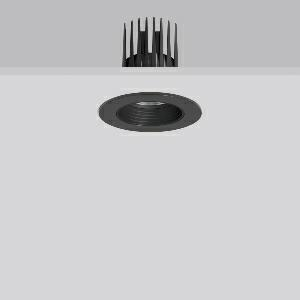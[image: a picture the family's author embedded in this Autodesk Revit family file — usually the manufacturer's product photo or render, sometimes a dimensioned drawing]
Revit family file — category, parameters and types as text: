
# Revit family: heledon_mini_e_901746_003_76_7caa
name_source: partatom
category: Lighting Fixtures
units: mm (PartAtom-declared; Revit-internal decimal feet)

## family parameters
Cut with Voids When Loaded = No
Host = Face
Light Source = No
Part Type = Normal
Room Calculation Point = No
Round Connector Dimension = Use Diameter
Shared = No

## types (1)
- HELEDON mini E (1 x LED Modul 930, 2250 lm, 3000)
    Apparent Load = 20 VA
    Approval mark = CE
    CIE Flux Codes = 80 99 100 100 100
    Color Rendering = 90
    Color Temperature = 3000
    Default Elevation = 1800 mm
    Description = Series: HELEDON mini
Round recessed downlight. Housing: die-cast aluminium, powder-coated. Black plastic ring and recessed LED to prevent glare from the side. Optical assembly with lens made of plastic (polycarbonate) for the best homogeneous light distribution - can be changed without tools. Best colour rendering index Ra>90. Suitable for Recessed ceiling mounting. Installation without tools thanks to spring fastening system. Including separate LED converter with connecting cable 600 mm.High quality converter without flickering and stroboscopic effect. Through-wiring box (5 pole) available as accessory. The following accessories can be mounted without use of tools: interchangeable lenses, decorative glasses, honeycomb louvre, clear and frosted diffusers, white interchangeable plastic ring. 
Colour: deep black, matt (RAL 9005)
Diameter: 124 mm
Height: 3 mm
Cut-out diameter: 114 mm
Recess height: 170 mm
Luminaire: recess height: 120 mm
Lamp: LED
Socket: without socket
Colour temperature: 3000K
Colour rendering index (CRI): 92
System power: 20 W
Rated luminous flux: 2250 lm
Luminous efficiency: 113 lm/W
Control gear: Converter, dimmable, DALI
Protection class: II
Type of protection: IP 20
    Height = 0 mm  [stored 0 ft]
    Lamp = 1 x LED Modul 930
    Lamp Light Flux = 2250 lm
    Lamp count = 1
    Length = 124 mm  [stored 0.406824 ft]
    Lifetime = 50000 h
    Luminous efficacy = 113 lm/W
    Manufacturer = RZB
    ModVariant = No
    Model = 901746.003.76
    Mounting Place = Ceiling
    Mounting Type = Recessed
    Number of Poles = 1
    OnlyDefault = Yes
    Power Factor = 1
    Product Name = HELEDON mini E
    Product group = Recessed downlights
    ProductGroupID = 402
    Protection Class = Protection class II
    Protection Degree = IP 20
    RLX_Detail_Level = 1
    RLX_Emergency_Light_Flux = 0 lm
    RLX_Emergency_Type = 0
    RLX_Emergency_Type_DB = No
    RlxData = <blob elided: 125225 chars, md5=127bc0c8>
    Socket = socket
    Standby Power = 0 W
    System Light Flux = 2250 lm
    System Power = 20 W
    Type Comments = Product without accessories
    Type Image = 901656.003.jpg
    URL = http://relux.com
    VarID = ---
    Voltage = 230 V
    Voltage Range = 220-240 V
    Weight = 0.00 kg
    Width = 0 mm  [stored 0 ft]

note: [stored X ft] marks values corroborated as IEEE doubles in the binary element streams (Revit-internal decimal feet)

## geometry (parser evidence)
native form markers: Blend x4, Sweep x11
no freeform markers — native parametric forms only
